# Revit family: Faucet-Handle-KOHLER-Triton-K-16012
name_source: partatom
category: Plumbing Fixtures
revit_build: Autodesk Revit 2017 (Build: 20160225_1515(x64)
units: mm (PartAtom-declared; Revit-internal decimal feet)

## family parameters
Cut with Voids When Loaded = No
Host = Face
OmniClass Number = 23.31.11.00
Part Type = Normal
Room Calculation Point = No
Round Connector Dimension = Use Diameter
Shared = No

## types (4) — shared parameters
Assembly Code = D2010
Blue Indexing = Kohler-Metal-Blue
CW Connection = Yes
Cold Water Inlet = Cold Water Inlet
Date Modified = 08/17/2021
Default Elevation = 36"
Drain Included = No
Finish = Kohler-Metal-CP-Polished_Chrome
Flow Rate = 0 GPM
HW Connection = Yes
Hot Water Inlet = Hot Water Inlet
Manufacturer = KOHLER Co.
Master Format 2014 = 22 41 39
Master Format 2014 Name = Residential Faucets, Supplies, and Trim
Material = Solid Brass Construction
Pressure = 0.00 psi
Product Documentation Link = https://www.us.kohler.com
Product Name = Triton
Product Page URL = http://www.us.kohler.com
Red Indexing = Kohler-Metal-Red
URL = https://www.us.kohler.com
Vent Connection = No
Waste Connection = No
Waste Water Outlet = Waste Water Outlet
WaterSense Certified = No

## per-type parameters (varying)
| type | ADA Compliant | Cross Handle | Description | Distance | Handle Clearance | Height | Length | Lever Handle | Model | Standard Handle | Type | Wristblade Lever Handle |
| Standard Handle, CP-Polished Chrome | No | No | Standard handles for widespread base faucet | 1 5/8" | 1 7/16" | 1 5/8" | 1 5/8" | No | K-16012-2-CP | Yes | 1 | No |
| Cross Handle, CP-Polished Chrome | Yes | Yes | Cross handles for widespread base faucet | 1 11/16" | 1 7/16" | 2 1/8" | 1 11/16" | No | K-16012-3-CP | No | 2 | No |
| Lever Handle, CP-Polished Chrome | Yes | No | Lever handles for widespread base faucet | 1 11/16" | 2 7/16" | 2 1/8" | 1 11/16" | Yes | K-16012-4-CP | No | 3 | No |
| Wristblade Lever Handle, CP-Polished Chrome | Yes | No | Wristblade lever handles for widespread base faucet | 1 3/4" | 4" | 3 3/8" | 1 3/4" | No | K-16012-5-CP | No | 4 | Yes |

## geometry (parser evidence)
native form markers: Sweep x5
no freeform markers — native parametric forms only
